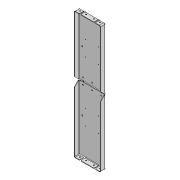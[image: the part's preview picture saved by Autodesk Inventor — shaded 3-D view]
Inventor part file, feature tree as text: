
AUTODESK INVENTOR PART (.ipt)
format: ipt  version: 2020 (Build 240168000, 168)  size: 262,144 bytes
history: native  units: mm
features: other x4, projected_geometry x2, extrude x1, sketch x1
ambient origin geometry x8: Origin, YZ Plane, XZ Plane, XY Plane, X Axis, Y Axis, Z Axis, Center Point
bodies: Body1 (feature_tree)
feature tree (8):
  other  "Display_Mount_AB.iam"
  other  "Display_Angle.ipt:1"
  other  "Display_Angle_B.ipt:1"
  other  "ソリッド1"
  extrude  "押し出し1"  Depth=10.0mm
  sketch  "スケッチ1"
  projected_geometry  "投影ループ1"
  projected_geometry  "投影ループ2"
